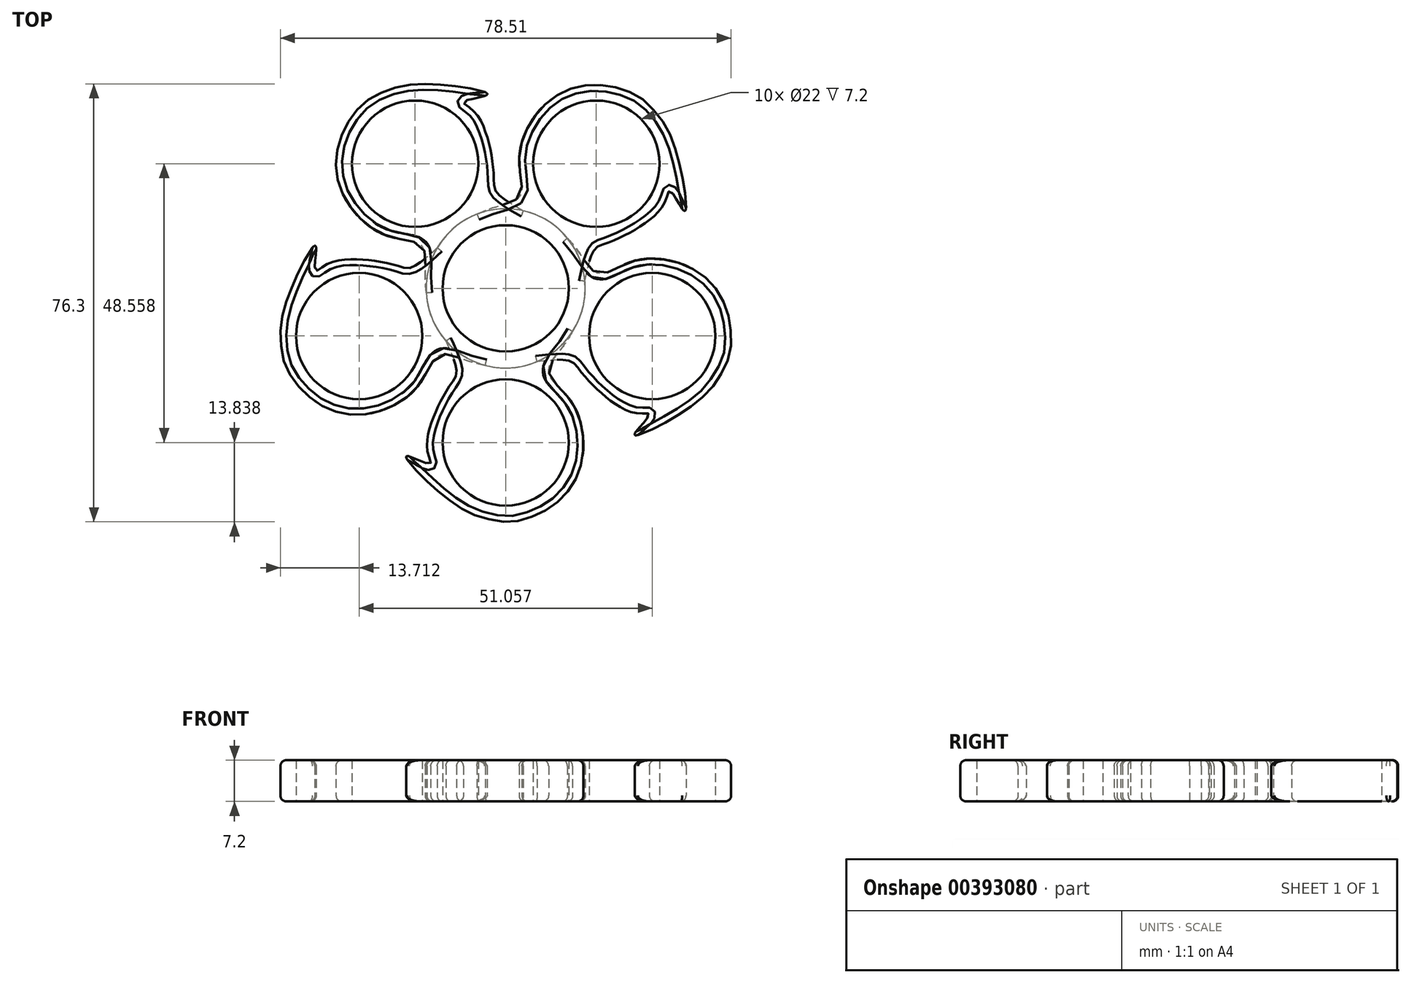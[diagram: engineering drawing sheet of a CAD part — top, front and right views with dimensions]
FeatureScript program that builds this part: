
annotation { "Feature Type Name" : "Feature", "Feature Type Description" : "" }
export const myFeature = defineFeature(function(context is Context, id is Id, definition is map)
    precondition{}
    {
        {
            var Q0;
            Q0=qCreatedBy(makeId("Top.planeOp"),FACE);
            var sketch = newSketch(context, id + "F0", { "sketchPlane" : qUnion([Q0])});
            skCircle(sketch, "E0", {"center": v(0, 0) * mm, "radius": 11 * mm});
            skCircle(sketch, "E1", {"center": v(0, -26.84) * mm, "radius": 11 * mm});
            skCircle(sketch, "E2", {"center": v(0, 0) * mm, "radius": 13.86 * mm});
            skLineSegment(sketch, "E3", {"start": v(0, 0) * mm, "end": v(0, -53.68) * mm, "construction": true});
            skFitSpline(sketch, "E4", {"points": [v(11.65, -7.52) * mm, v(9.7, -10.52) * mm, v(7.48, -14.55) * mm, v(11.48, -19.8) * mm, v(13.37, -29.5) * mm, v(10.69, -35.54) * mm, v(6.87, -38.72) * mm, v(2.5, -40.42) * mm, v(-0.17, -40.67) * mm, v(-3.15, -40.17) * mm, v(-9.64, -37.02) * mm, v(-17.24, -29.21) * mm, v(-13.24, -30.62) * mm, v(-13.7, -27.85) * mm, v(-9.88, -17.15) * mm, v(-8.54, -14.62) * mm, v(-10.42, -9.14) * mm], "startDerivative": vector(-32.29, -56) * mm, "endDerivative": vector(-44.62, 97.98) * mm});
            skSolve(sketch);
        }
        {
            var Q0;
            Q0 = qSketchRegion(id + "F0", true);
            extrude(context, id + "F1", {"entities" : qUnion([Q0]), "depth" : 7.2 * mm});
        }
        {
            var Q0;
            Q0=makeQuery(id+"F1.opExtrude","CAP_EDGE",EDGE,{"disambiguationData":[OSD([sQuery(id+"F0.wireOp",EDGE,"E4")])],"isStart":true});
            var Q1;
            Q1=makeQuery(id+"F1.opExtrude","CAP_EDGE",EDGE,{"disambiguationData":[OSD([sQuery(id+"F0.wireOp",EDGE,"E2")])],"isStart":true});
            var Q2;
            Q2=makeQuery(id+"F1.opExtrude","CAP_EDGE",EDGE,{"disambiguationData":[OSD([sQuery(id+"F0.wireOp",EDGE,"E4")])],"isStart":false});
            var Q3;
            Q3=makeQuery(id+"F1.opExtrude","CAP_EDGE",EDGE,{"disambiguationData":[OSD([sQuery(id+"F0.wireOp",EDGE,"E2")])],"isStart":false});
            fillet(context, id + "F2", {"entities" : qUnion([Q0, Q1, Q2, Q3]), "radius" : 1.02 * mm, "tangentPropagation" : true, "allowEdgeOverflow" : false});
        }
        {
            var Q0;
            Q0=makeQuery(id+"F1.opExtrude","SWEPT_BODY",BODY,{"disambiguationData":[OSD([sQuery(id+"F0.wireOp",EDGE,"E0"),sQuery(id+"F0.wireOp",EDGE,"E1"),sQuery(id+"F0.wireOp",EDGE,"E2"),sQuery(id+"F0.wireOp",EDGE,"E4")])]});
            var Q1;
            Q1=makeQuery(id+"F1.opExtrude","CAP_EDGE",EDGE,{"disambiguationData":[OSD([sQuery(id+"F0.wireOp",EDGE,"E0")])],"isStart":false});
            circularPattern(context, id + "F3", {"entities" : qUnion([Q0]), "axis" : qUnion([Q1]), "angle" : 360 * degree, "instanceCount" : 5, "oppositeDirection" : true, "equalSpace" : true});
        }
    });
